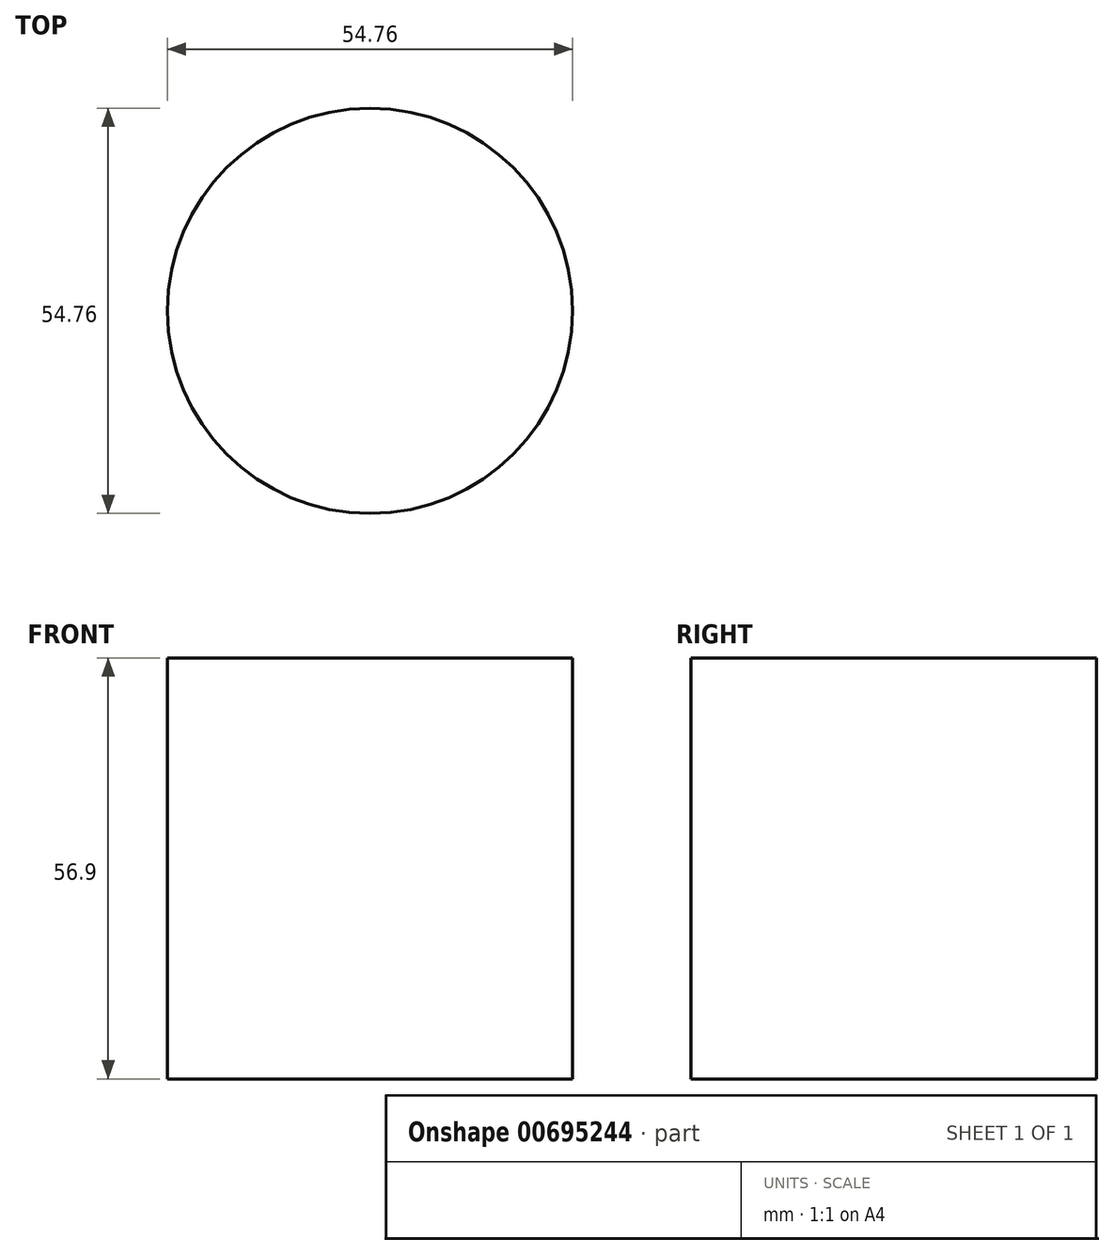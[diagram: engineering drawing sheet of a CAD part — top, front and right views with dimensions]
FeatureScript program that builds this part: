
annotation { "Feature Type Name" : "Feature", "Feature Type Description" : "" }
export const myFeature = defineFeature(function(context is Context, id is Id, definition is map)
    precondition{}
    {
        {
            var Q0;
            Q0=qCreatedBy(makeId("Top.planeOp"),FACE);
            var sketch = newSketch(context, id + "F0", { "sketchPlane" : qUnion([Q0])});
            skCircle(sketch, "E0", {"center": v(0, 0) * mm, "radius": 27.38 * mm});
            skSolve(sketch);
        }
        {
            var Q0;
            Q0 = qSketchRegion(id + "F0", true);
            extrude(context, id + "F1", {"entities" : qUnion([Q0]), "depth" : 56.9 * mm, "offsetDistance" : 25.4 * mm});
        }
    });
